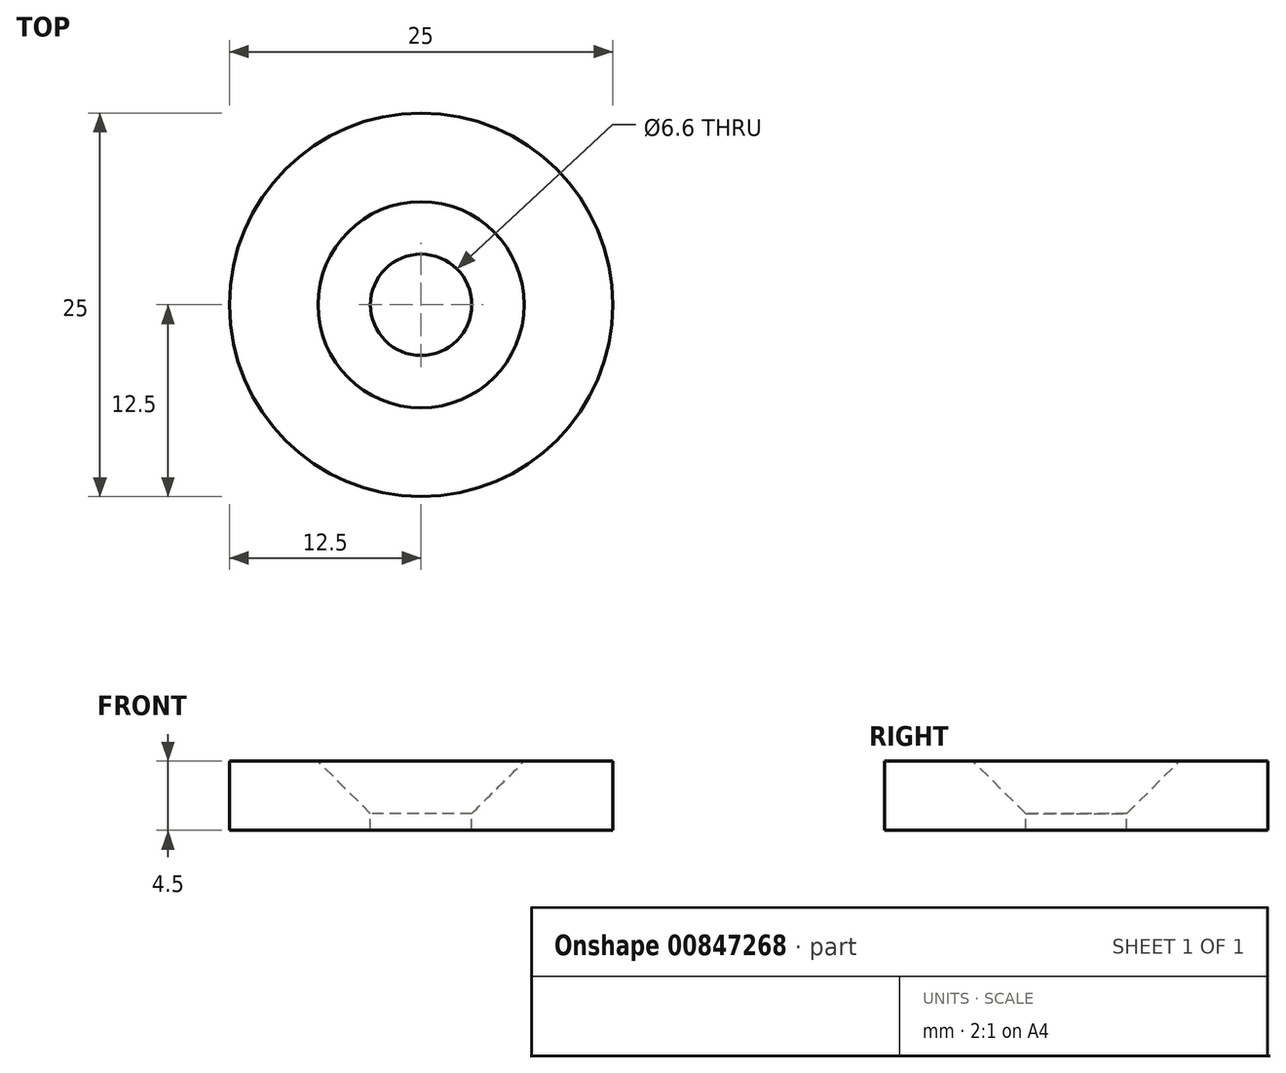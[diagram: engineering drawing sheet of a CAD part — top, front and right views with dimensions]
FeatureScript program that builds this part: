
annotation { "Feature Type Name" : "Feature", "Feature Type Description" : "" }
export const myFeature = defineFeature(function(context is Context, id is Id, definition is map)
    precondition{}
    {
        {
            var Q0;
            Q0=qCreatedBy(makeId("Top.planeOp"),FACE);
            var sketch = newSketch(context, id + "F0", { "sketchPlane" : qUnion([Q0])});
            skCircle(sketch, "E0", {"center": v(0, 0) * mm, "radius": 12.5 * mm});
            skSolve(sketch);
        }
        {
            var Q0;
            Q0=makeQuery(id+"F0.imprint","IMPRINT",FACE,{"disambiguationData":[TD([[makeQuery(id+"F0.imprint","IMPRINT",EDGE,{"derivedFrom":sQuery(id+"F0.wireOp",EDGE,"E0")}),1.0]])]});
            extrude(context, id + "F1", {"entities" : qUnion([Q0]), "depth" : 4.5 * mm, "offsetDistance" : 25 * mm});
        }
        {
            var Q0;
            Q0=makeQuery(id+"F1.opExtrude","CAP_FACE",FACE,{"disambiguationData":[OSD([sQuery(id+"F0.wireOp",EDGE,"E0")])],"isStart":false});
            var sketch = newSketch(context, id + "F2", { "sketchPlane" : qUnion([Q0])});
            skPoint(sketch, "E1", {"position": v(0, 0) * mm});
            skSolve(sketch);
        }
        {
            var Q0;
            Q0=sQuery(id+"F2.wireOp",VERTEX,"E1");
            var Q1;
            Q1=makeQuery(id+"F1.opExtrude","SWEPT_BODY",BODY,{"disambiguationData":[OSD([sQuery(id+"F0.wireOp",EDGE,"E0")])]});
            hole(context, id + "F3", {"style" : HoleStyle.C_SINK, "endStyle" : HoleEndStyle.THROUGH, "standardTappedOrClearance" : lookupTablePath({ "fit" : "Normal", "standard" : "ISO", "size" : "M6", "type" : "Clearance" }), "standardBlindInLast" : lookupTablePath({ "fit" : "Standard", "standard" : "ISO", "size" : "M6", "type" : "Clearance" }), "holeDiameter" : 6.6 * mm, "cSinkDiameter" : 13.44 * mm, "cSinkAngle" : 90 * degree, "majorDiameter" : 5 * mm, "isTappedThrough" : true, "tappedDepth" : 12 * mm, "tapClearance" : 3, "locations" : qUnion([Q0]), "scope" : qUnion([Q1])});
        }
    });
